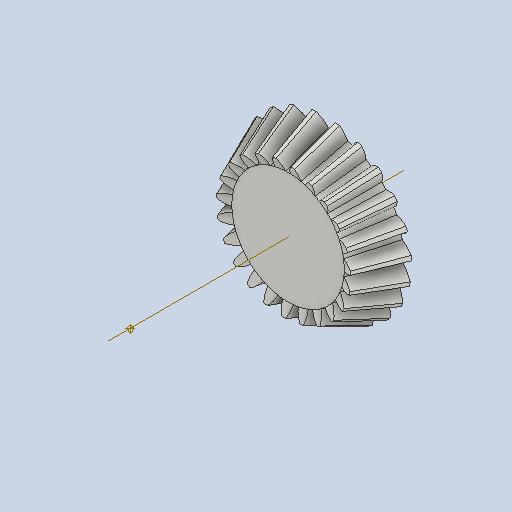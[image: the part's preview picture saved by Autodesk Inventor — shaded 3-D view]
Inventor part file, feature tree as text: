
AUTODESK INVENTOR PART (.ipt)
format: ipt  version: 2024 (Build 280153000, 153)  size: 560,640 bytes
history: native  units: mm
features: other x24, loft x2, pattern_circular x2
ambient origin geometry x6: Origin, XZ Plane, X Axis, Y Axis, Z Axis, Center Point
bodies: Solid1 (feature_tree)
feature tree (28):
  other  "Top Point"
  other  "Mesh Plane2"
  other  "Teeth Body"
  other  "Start Point"
  other  "Tooth Plane"
  other  "Start Sketch"
  other  "End Point"
  other  "3D Sketch Right"
  other  "End Plane Right"
  loft  "Loft Right"
  pattern_circular  "Circular Pattern Right"  [2 undecoded]
  other  "3D Sketch Left"
  other  "End Plane Left"
  loft  "Loft Left"
  pattern_circular  "Circular Pattern Left"  Count=2  [1 undecoded]
  other  "Fix Body"
  other  "Mesh Plane"
  other  "Top Plane"
  other  "Teeth Body Sketch"
  other  "End Plane"
  other  "End Sketch"
  other  "Helical Curve Left"
  other  "End Sketch Left"
  other  "Body Sketch"
  other  "Srf1"
  other  "Helical Curve Right"
  other  "End Sketch Right"
  other  "Pitch Diameter"
note: 3 required parameter values undecoded (feature->parameter linkage not recoverable at this tier; creation-order binding heuristic only, values carry confidence <= 0.55)
